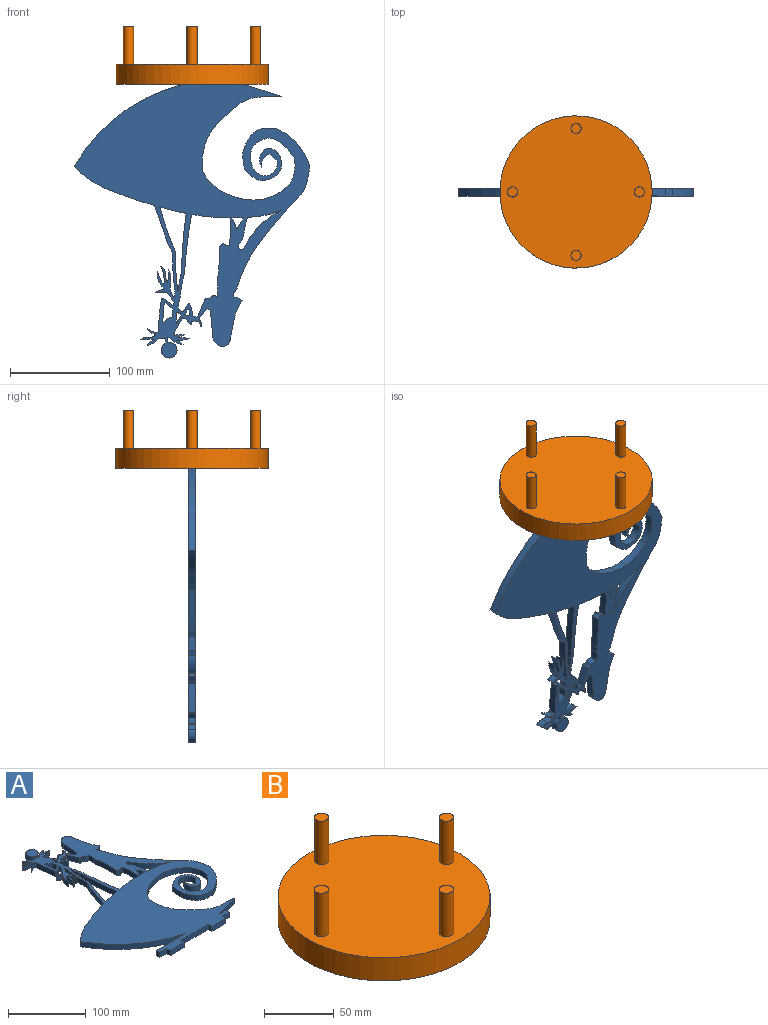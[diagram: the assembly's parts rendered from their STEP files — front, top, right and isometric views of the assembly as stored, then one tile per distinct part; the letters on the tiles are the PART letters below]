
ASSEMBLY  parts=2 mates=1
PART A: 176 faces, bbox 235.7x286.5x7.9 mm
  f0: plane 20.52x7.94mm, normal (1,0.08,0), area 163.3mm2, adj f1,f173,f174,f175
  f1: cylinder r=36.86mm len=9.55mm, axis (0,0,-1), area 89.6mm2, adj f0,f2,f174,f175
  f2: cylinder r=43.14mm len=7.94mm, axis (0,0,-1), area 60.5mm2, adj f1,f173,f174,f175
  f3: plane 10.27x7.94mm, normal (1,0,0), area 81.5mm2, adj f4,f166,f174,f175
  f4: plane 7.94x7.71mm, normal (-0.85,-0.52,0), area 71.6mm2, adj f3,f166,f174,f175
  f5: cylinder r=227.24mm len=11.79mm, axis (0,0,-1), area 93.6mm2, adj f6,f167,f174,f175
  f6: cylinder r=44.33mm len=12.07mm, axis (0,0,-1), area 103.8mm2, adj f5,f167,f174,f175
  f7: cylinder r=337.12mm len=43.63mm, axis (0,0,-1), area 366.7mm2, adj f8,f168,f174,f175
  f8: cylinder r=9.96mm len=7.94mm, axis (0,0,-1), area 34.1mm2, adj f7,f9,f174,f175
  f9: cylinder r=196.99mm len=36.66mm, axis (0,0,-1), area 292mm2, adj f8,f10,f174,f175
  f10: cylinder r=415.23mm len=16.03mm, axis (0,0,-1), area 129.1mm2, adj f9,f11,f174,f175
  f11: cylinder r=48.21mm len=7.94mm, axis (0,0,-1), area 61.4mm2, adj f10,f12,f174,f175
  f12: cylinder r=479.52mm len=54.44mm, axis (0,0,-1), area 433.9mm2, adj f11,f13,f174,f175
  f13: cylinder r=227.24mm len=7.94mm, axis (0,0,-1), area 19mm2, adj f12,f168,f174,f175
  f14: plane 17.78x7.94mm, normal (-0.92,-0.38,0), area 152.8mm2, adj f15,f169,f174,f175
  f15: cylinder r=1.27mm len=7.94mm, axis (0,0,-1), area 13.1mm2, adj f14,f16,f174,f175
  f16: plane 7.94x3.29mm, normal (0.12,-0.99,0), area 26.3mm2, adj f15,f17,f174,f175
  f17: cylinder r=5.3mm len=7.94mm, axis (0,0,-1), area 69.4mm2, adj f16,f18,f174,f175
  f18: cylinder r=24.79mm len=10.48mm, axis (0,0,-1), area 83.9mm2, adj f17,f19,f174,f175
  f19: cylinder r=16.53mm len=7.94mm, axis (0,0,-1), area 44mm2, adj f18,f20,f174,f175
  f20: cylinder r=158.24mm len=34.32mm, axis (0,0,-1), area 273.3mm2, adj f19,f21,f174,f175
  f21: cylinder r=9.12mm len=7.94mm, axis (0,0,-1), area 41.4mm2, adj f20,f22,f174,f175
  f22: cylinder r=7mm len=7.94mm, axis (0,0,-1), area 52.5mm2, adj f21,f23,f174,f175
  f23: cylinder r=99.7mm len=27.95mm, axis (0,0,-1), area 222.8mm2, adj f22,f24,f174,f175
  f24: cylinder r=227.24mm len=38.58mm, axis (0,0,-1), area 307.8mm2, adj f23,f25,f174,f175
  f25: cylinder r=488.64mm len=56.23mm, axis (0,0,-1), area 450mm2, adj f24,f26,f174,f175
  f26: cylinder r=37.95mm len=7.94mm, axis (0,0,-1), area 50mm2, adj f25,f27,f174,f175
  f27: cylinder r=89.95mm len=19.2mm, axis (0,0,-1), area 155mm2, adj f26,f28,f174,f175
  f28: cylinder r=46.77mm len=13.1mm, axis (0,0,-1), area 105.7mm2, adj f27,f29,f174,f175
  f29: plane 7.94x3.21mm, normal (0.58,-0.81,0), area 31.3mm2, adj f28,f30,f174,f175
  f30: cylinder r=1.57mm len=7.94mm, axis (0,0,-1), area 20.4mm2, adj f29,f31,f174,f175
  f31: plane 7.94x7.65mm, normal (-0.85,-0.52,0), area 71.1mm2, adj f30,f32,f174,f175
  f32: cylinder r=0.51mm len=7.94mm, axis (0,0,-1), area 8.2mm2, adj f31,f33,f174,f175
  f33: cylinder r=19.29mm len=12.67mm, axis (0,0,-1), area 105mm2, adj f32,f169,f174,f175
  f34: cylinder r=352.42mm len=52.1mm, axis (0,0,-1), area 538.1mm2, adj f35,f170,f174,f175
  f35: cylinder r=120.39mm len=36.06mm, axis (0,0,-1), area 316.5mm2, adj f34,f36,f174,f175
  f36: cylinder r=14.19mm len=7.94mm, axis (0,0,-1), area 44.1mm2, adj f35,f37,f174,f175
  f37: cylinder r=9.85mm len=7.94mm, axis (0,0,-1), area 44.6mm2, adj f36,f38,f174,f175
  f38: cylinder r=14.52mm len=9.3mm, axis (0,0,-1), area 81.1mm2, adj f37,f39,f174,f175
  f39: cylinder r=0.25mm len=7.94mm, axis (0,0,-1), area 3mm2, adj f38,f40,f174,f175
  f40: cylinder r=40.75mm len=17.83mm, axis (0,0,-1), area 157.1mm2, adj f39,f41,f174,f175
  f41: plane 21.3x7.94mm, normal (0.98,0.18,0), area 172.1mm2, adj f40,f42,f174,f175
  f42: cylinder r=7.87mm len=11.54mm, axis (0,0,-1), area 118.1mm2, adj f41,f43,f174,f175
  f43: cylinder r=11.53mm len=9.08mm, axis (0,0,-1), area 89.5mm2, adj f42,f44,f174,f175
  f44: plane 26.31x7.94mm, normal (-1,0.09,0), area 209.7mm2, adj f43,f45,f174,f175
  f45: cylinder r=6.34mm len=7.94mm, axis (0,0,-1), area 30.2mm2, adj f44,f46,f174,f175
  f46: plane 9.22x7.94mm, normal (0.79,0.62,0), area 93.1mm2, adj f45,f47,f174,f175
  f47: cylinder r=2.32mm len=7.94mm, axis (0,0,-1), area 26.8mm2, adj f46,f48,f174,f175
  f48: cylinder r=5.13mm len=7.94mm, axis (0,0,-1), area 48.7mm2, adj f47,f49,f174,f175
  f49: cylinder r=0.25mm len=7.94mm, axis (0,0,-1), area 5.2mm2, adj f48,f50,f174,f175
  f50: cylinder r=8.39mm len=7.94mm, axis (0,0,-1), area 39.4mm2, adj f49,f51,f174,f175
  f51: cylinder r=2.08mm len=7.94mm, axis (0,0,-1), area 8mm2, adj f50,f52,f174,f175
  f52: cylinder r=8.25mm len=7.94mm, axis (0,0,-1), area 44.8mm2, adj f51,f53,f174,f175
  f53: cylinder r=1.21mm len=7.94mm, axis (0,0,-1), area 13.3mm2, adj f52,f54,f174,f175
  f54: cylinder r=4.68mm len=7.94mm, axis (0,0,-1), area 12.8mm2, adj f53,f55,f174,f175
  f55: cylinder r=0.25mm len=7.94mm, axis (0,0,-1), area 5mm2, adj f54,f56,f174,f175
  f56: cylinder r=7.88mm len=7.94mm, axis (0,0,-1), area 43.2mm2, adj f55,f57,f174,f175
  f57: cylinder r=6.68mm len=7.94mm, axis (0,0,-1), area 47.5mm2, adj f56,f58,f174,f175
  f58: plane 14.05x8.18mm, normal (0.86,0.5,0), area 129mm2, adj f57,f59,f174,f175
  f59: cylinder r=4.51mm len=7.94mm, axis (0,0,-1), area 31.1mm2, adj f58,f60,f174,f175
  f60: cylinder r=20.93mm len=9.94mm, axis (0,0,-1), area 80.1mm2, adj f59,f61,f174,f175
  f61: cylinder r=25.41mm len=7.94mm, axis (0,0,-1), area 56.6mm2, adj f60,f62,f174,f175
  f62: cylinder r=36.23mm len=11.63mm, axis (0,0,-1), area 92.8mm2, adj f61,f63,f174,f175
  f63: cylinder r=28.67mm len=13.4mm, axis (0,0,-1), area 108.3mm2, adj f62,f64,f174,f175
  f64: cylinder r=20.22mm len=7.94mm, axis (0,0,-1), area 66.6mm2, adj f63,f65,f174,f175
  f65: cylinder r=12.82mm len=9.56mm, axis (0,0,-1), area 82.4mm2, adj f64,f66,f174,f175
  f66: cylinder r=11.48mm len=7.94mm, axis (0,0,-1), area 55.9mm2, adj f65,f67,f174,f175
  f67: cylinder r=12.66mm len=7.94mm, axis (0,0,-1), area 38.3mm2, adj f66,f68,f174,f175
  f68: cylinder r=7.89mm len=15.77mm, axis (0,0,-1), area 375.3mm2, adj f67,f69,f174,f175
  f69: cylinder r=14.9mm len=7.94mm, axis (0,0,-1), area 33.3mm2, adj f68,f70,f174,f175
  f70: plane 7.94x7.28mm, normal (0.02,1,0), area 57.8mm2, adj f69,f71,f174,f175
  f71: cylinder r=20.94mm len=10.93mm, axis (0,0,-1), area 102.6mm2, adj f70,f72,f174,f175
  f72: cylinder r=11.14mm len=7.94mm, axis (0,0,-1), area 60.5mm2, adj f71,f73,f174,f175
  f73: cylinder r=0.83mm len=7.94mm, axis (0,0,-1), area 19.2mm2, adj f72,f74,f174,f175
  f74: cylinder r=57.07mm len=11.86mm, axis (0,0,-1), area 94.5mm2, adj f73,f75,f174,f175
  f75: cylinder r=8.74mm len=7.94mm, axis (0,0,-1), area 66.6mm2, adj f74,f76,f174,f175
  f76: cylinder r=10.18mm len=7.94mm, axis (0,0,-1), area 51.8mm2, adj f75,f77,f174,f175
  f77: cylinder r=1.22mm len=7.94mm, axis (0,0,-1), area 23.7mm2, adj f76,f78,f174,f175
  f78: cylinder r=10.13mm len=7.94mm, axis (0,0,-1), area 72.3mm2, adj f77,f79,f174,f175
  f79: cylinder r=23.9mm len=9.43mm, axis (0,0,-1), area 82mm2, adj f78,f80,f174,f175
  f80: cylinder r=1.6mm len=7.94mm, axis (0,0,-1), area 21.9mm2, adj f79,f81,f174,f175
  f81: cylinder r=285.45mm len=31.77mm, axis (0,0,-1), area 253.3mm2, adj f80,f82,f174,f175
  f82: cylinder r=1.27mm len=7.94mm, axis (0,0,-1), area 20.6mm2, adj f81,f83,f174,f175
  f83: plane 10.37x7.94mm, normal (0.58,-0.81,0), area 101.1mm2, adj f82,f84,f174,f175
  f84: cylinder r=70.21mm len=7.94mm, axis (0,0,-1), area 24.5mm2, adj f83,f85,f174,f175
  f85: cylinder r=50.8mm len=10.09mm, axis (0,0,-1), area 99.4mm2, adj f84,f86,f174,f175
  f86: plane 10.81x7.94mm, normal (0,1,0), area 85.8mm2, adj f85,f87,f174,f175
  f87: cylinder r=8.25mm len=7.94mm, axis (0,0,-1), area 56.7mm2, adj f86,f88,f174,f175
  f88: cylinder r=1.04mm len=7.94mm, axis (0,0,-1), area 19.5mm2, adj f87,f89,f174,f175
  f89: cylinder r=20mm len=16.63mm, axis (0,0,-1), area 144mm2, adj f88,f90,f174,f175
  f90: cylinder r=75.46mm len=11.84mm, axis (0,0,-1), area 102mm2, adj f89,f91,f174,f175
  f91: cylinder r=0.82mm len=7.94mm, axis (0,0,-1), area 16.9mm2, adj f90,f92,f174,f175
  f92: cylinder r=35.56mm len=16.89mm, axis (0,0,-1), area 137.6mm2, adj f91,f93,f174,f175
  f93: cylinder r=9.62mm len=7.94mm, axis (0,0,-1), area 59.7mm2, adj f92,f94,f174,f175
  f94: cylinder r=29.77mm len=7.94mm, axis (0,0,-1), area 52.9mm2, adj f93,f95,f174,f175
  f95: cylinder r=10.97mm len=7.94mm, axis (0,0,-1), area 32.8mm2, adj f94,f96,f174,f175
  f96: cylinder r=43.01mm len=12.61mm, axis (0,0,-1), area 101.1mm2, adj f95,f97,f174,f175
  f97: cylinder r=12.3mm len=7.94mm, axis (0,0,-1), area 51.1mm2, adj f96,f98,f174,f175
  f98: cylinder r=141.13mm len=14.24mm, axis (0,0,-1), area 113.2mm2, adj f97,f99,f174,f175
  f99: cylinder r=36.5mm len=7.94mm, axis (0,0,-1), area 63.6mm2, adj f98,f100,f174,f175
  f100: cylinder r=3.1mm len=7.94mm, axis (0,0,-1), area 20.6mm2, adj f99,f101,f174,f175
  f101: cylinder r=70.21mm len=7.94mm, axis (0,0,-1), area 43.9mm2, adj f100,f102,f174,f175
  f102: cylinder r=261.17mm len=37.18mm, axis (0,0,-1), area 295.8mm2, adj f101,f103,f174,f175
  f103: cylinder r=55.57mm len=11.58mm, axis (0,0,-1), area 102.5mm2, adj f102,f104,f174,f175
  f104: plane 35.51x12.47mm, normal (-0.94,0.33,0), area 298.7mm2, adj f103,f105,f174,f175
  f105: cylinder r=445.39mm len=49.93mm, axis (0,0,-1), area 420.4mm2, adj f104,f106,f174,f175
  f106: cylinder r=85.22mm len=30.36mm, axis (0,0,-1), area 298.1mm2, adj f105,f107,f174,f175
  f107: cylinder r=172.99mm len=108.34mm, axis (0,0,-1), area 1109.1mm2, adj f106,f108,f174,f175
  f108: plane 54x7.94mm, normal (0,1,0), area 428.6mm2, adj f107,f109,f174,f175
  f109: plane 7.94x6.35mm, normal (-1,0,0), area 50.4mm2, adj f108,f110,f174,f175
  f110: plane 12.7x7.94mm, normal (0,-1,0), area 100.8mm2, adj f109,f111,f174,f175
  f111: plane 7.94x6.35mm, normal (-1,0,0), area 50.4mm2, adj f110,f112,f174,f175
  f112: plane 25.4x7.94mm, normal (0,-1,0), area 201.6mm2, adj f111,f113,f174,f175
  f113: plane 7.94x6.35mm, normal (1,0,0), area 50.4mm2, adj f112,f114,f174,f175
  f114: plane 50.8x7.94mm, normal (0,-1,0), area 403.2mm2, adj f113,f115,f174,f175
  f115: plane 7.94x6.35mm, normal (-1,0,0), area 50.4mm2, adj f114,f116,f174,f175
  f116: plane 25.4x7.94mm, normal (0,-1,0), area 201.6mm2, adj f115,f117,f174,f175
  f117: plane 7.94x6.35mm, normal (1,0,0), area 50.4mm2, adj f116,f118,f174,f175
  f118: plane 12.7x7.94mm, normal (0,-1,0), area 100.8mm2, adj f117,f119,f174,f175
  f119: plane 7.94x6.35mm, normal (1,0,0), area 50.4mm2, adj f118,f120,f174,f175
  f120: plane 11.56x7.94mm, normal (0,1,0), area 91.8mm2, adj f119,f121,f174,f175
  f121: plane 38.12x11.95mm, normal (0.3,-0.95,0), area 317.1mm2, adj f120,f122,f174,f175
  f122: plane 21.78x7.94mm, normal (0.03,1,0), area 173mm2, adj f121,f123,f174,f175
  f123: cylinder r=37.94mm len=21.74mm, axis (0,0,-1), area 186.1mm2, adj f122,f124,f174,f175
  f124: cylinder r=179.29mm len=19.92mm, axis (0,0,-1), area 211.2mm2, adj f123,f125,f174,f175
  f125: cylinder r=57.58mm len=49.12mm, axis (0,0,-1), area 424.3mm2, adj f124,f126,f174,f175
  f126: cylinder r=42.38mm len=19.79mm, axis (0,0,-1), area 219.2mm2, adj f125,f127,f174,f175
  f127: cylinder r=79.8mm len=22.23mm, axis (0,0,-1), area 188.1mm2, adj f126,f128,f174,f175
  f128: cylinder r=50.17mm len=15.51mm, axis (0,0,-1), area 123.7mm2, adj f127,f129,f174,f175
  f129: cylinder r=47.79mm len=27.94mm, axis (0,0,-1), area 250.3mm2, adj f128,f130,f174,f175
  f130: cylinder r=25.95mm len=13.94mm, axis (0,0,-1), area 127.2mm2, adj f129,f131,f174,f175
  f131: cylinder r=36.6mm len=14.64mm, axis (0,0,-1), area 117mm2, adj f130,f132,f174,f175
  f132: cylinder r=56.33mm len=16.26mm, axis (0,0,-1), area 177.7mm2, adj f131,f133,f174,f175
  f133: cylinder r=19.27mm len=13.59mm, axis (0,0,-1), area 114mm2, adj f132,f134,f174,f175
  f134: cylinder r=28.7mm len=8.69mm, axis (0,0,-1), area 78.2mm2, adj f133,f135,f174,f175
  f135: cylinder r=16.62mm len=10.59mm, axis (0,0,-1), area 98.7mm2, adj f134,f136,f174,f175
  f136: cylinder r=25.93mm len=10.49mm, axis (0,0,-1), area 84mm2, adj f135,f137,f174,f175
  f137: cylinder r=20.22mm len=7.94mm, axis (0,0,-1), area 66.2mm2, adj f136,f138,f174,f175
  f138: cylinder r=12.6mm len=16.26mm, axis (0,0,-1), area 142.9mm2, adj f137,f139,f174,f175
  f139: cylinder r=12.31mm len=12.9mm, axis (0,0,-1), area 119.4mm2, adj f138,f140,f174,f175
  f140: cylinder r=38.53mm len=7.94mm, axis (0,0,-1), area 78.2mm2, adj f139,f141,f174,f175
  f141: cylinder r=10.76mm len=12.96mm, axis (0,0,-1), area 136.7mm2, adj f140,f142,f174,f175
  f142: cylinder r=12.51mm len=16.18mm, axis (0,0,-1), area 140.2mm2, adj f141,f143,f174,f175
  f143: cylinder r=8.34mm len=8.05mm, axis (0,0,-1), area 69.3mm2, adj f142,f144,f174,f175
  f144: cylinder r=13.73mm len=9.03mm, axis (0,0,-1), area 97.6mm2, adj f143,f145,f174,f175
  f145: cylinder r=17.66mm len=11.91mm, axis (0,0,-1), area 96.7mm2, adj f144,f146,f174,f175
  f146: cylinder r=15.3mm len=10.2mm, axis (0,0,-1), area 114.6mm2, adj f145,f147,f174,f175
  f147: cylinder r=26.76mm len=12.66mm, axis (0,0,-1), area 102.1mm2, adj f146,f148,f174,f175
  f148: cylinder r=32.43mm len=13.82mm, axis (0,0,-1), area 135.4mm2, adj f147,f149,f174,f175
  f149: cylinder r=52.04mm len=17.76mm, axis (0,0,-1), area 142.9mm2, adj f148,f150,f174,f175
  f150: cylinder r=51.61mm len=14.68mm, axis (0,0,-1), area 127.1mm2, adj f149,f151,f174,f175
  f151: cylinder r=20.92mm len=11.08mm, axis (0,0,-1), area 114.4mm2, adj f150,f152,f174,f175
  f152: cylinder r=45.16mm len=14.96mm, axis (0,0,-1), area 119.5mm2, adj f151,f153,f174,f175
  f153: cylinder r=50.49mm len=13.17mm, axis (0,0,-1), area 118.6mm2, adj f152,f154,f174,f175
  f154: cylinder r=57.88mm len=31.34mm, axis (0,0,-1), area 307.7mm2, adj f153,f155,f174,f175
  f155: cylinder r=105.54mm len=23.2mm, axis (0,0,-1), area 189mm2, adj f154,f170,f174,f175
  f156: cylinder r=9.54mm len=7.94mm, axis (0,0,-1), area 55.6mm2, adj f157,f171,f174,f175
  f157: plane 7.94x5.45mm, normal (0.86,0.5,0), area 50.1mm2, adj f156,f171,f174,f175
  f158: cylinder r=80.87mm len=35.9mm, axis (0,0,-1), area 405.8mm2, adj f159,f172,f174,f175
  f159: cylinder r=60.69mm len=18.48mm, axis (0,0,-1), area 154.2mm2, adj f158,f160,f174,f175
  f160: cylinder r=227.24mm len=15.36mm, axis (0,0,-1), area 122.6mm2, adj f159,f161,f174,f175
  f161: cylinder r=109.18mm len=17.03mm, axis (0,0,-1), area 138.9mm2, adj f160,f162,f174,f175
  f162: cylinder r=28.03mm len=7.94mm, axis (0,0,-1), area 53.5mm2, adj f161,f163,f174,f175
  f163: cylinder r=21.61mm len=7.94mm, axis (0,0,-1), area 44.5mm2, adj f162,f164,f174,f175
  f164: cylinder r=2.54mm len=7.94mm, axis (0,0,-1), area 15mm2, adj f163,f165,f174,f175
  f165: cylinder r=7.26mm len=7.94mm, axis (0,0,-1), area 34.9mm2, adj f164,f172,f174,f175
  f166: cylinder r=4.71mm len=7.94mm, axis (0,0,-1), area 45.2mm2, adj f3,f4,f174,f175
  f167: cylinder r=82.29mm len=12.41mm, axis (0,0,-1), area 112.8mm2, adj f5,f6,f174,f175
  f168: cylinder r=445.39mm len=24.08mm, axis (0,0,-1), area 196.7mm2, adj f7,f13,f174,f175
  f169: cylinder r=21.13mm len=7.94mm, axis (0,0,-1), area 44.3mm2, adj f14,f33,f174,f175
  f170: cylinder r=60.69mm len=8.89mm, axis (0,0,-1), area 91.9mm2, adj f34,f155,f174,f175
  f171: cylinder r=8.45mm len=7.94mm, axis (0,0,-1), area 37.5mm2, adj f156,f157,f174,f175
  f172: cylinder r=25.34mm len=7.94mm, axis (0,0,-1), area 45.7mm2, adj f158,f165,f174,f175
  f173: plane 8.95x7.94mm, normal (-0.62,0.79,0), area 90.4mm2, adj f0,f2,f174,f175
  f174: plane 286.54x235.68mm, normal (0,0,1), area 23375.6mm2, adj f0,f1,f2,f3,f4,f5,f6,f7
  f175: plane 286.54x235.68mm, normal (0,0,-1), area 23375.6mm2, adj f0,f1,f2,f3,f4,f5,f6,f7
PART B: 24 faces, bbox 152.4x152.4x58.4 mm
  f0: plane 152.4x152.4mm, normal (0,0,-1), area 17172mm2, adj f1,f4,f6,f7,f8
  f1: cylinder r=76.2mm len=152.4mm, axis (0,0,-1), area 9728.8mm2, adj f0,f2
  f2: plane 152.4x152.4mm, normal (0,0,1), area 17917.2mm2, adj f1,f16,f18,f20,f22
  f3: plane 50.04x8.18mm, normal (0,0,-1), area 409.1mm2, adj f6,f7,f10,f14
  f4: plane 8.18x6.54mm, normal (1,0,0), area 53.5mm2, adj f0,f5,f6,f7
  f5: plane 14.22x8.18mm, normal (0,0,-1), area 116.3mm2, adj f4,f6,f7,f13
  f6: plane 130.81x13.08mm, normal (0,1,0), area 1197.8mm2, adj f0,f3,f4,f5,f8,f9,f10,f11
  f7: plane 130.81x13.08mm, normal (0,-1,0), area 1197.8mm2, adj f0,f3,f4,f5,f8,f9,f10,f11
  f8: plane 8.18x6.54mm, normal (-1,0,0), area 53.5mm2, adj f0,f6,f7,f9
  f9: plane 14.22x8.18mm, normal (0,0,-1), area 116.3mm2, adj f6,f7,f8,f11
  f10: plane 8.18x6.54mm, normal (1,0,0), area 53.5mm2, adj f3,f6,f7,f12
  f11: plane 8.18x6.54mm, normal (-1,0,0), area 53.5mm2, adj f6,f7,f9,f12
  f12: plane 26.16x8.18mm, normal (0,0,-1), area 213.9mm2, adj f6,f7,f10,f11
  f13: plane 8.18x6.54mm, normal (1,0,0), area 53.5mm2, adj f5,f6,f7,f15
  f14: plane 8.18x6.54mm, normal (-1,0,0), area 53.5mm2, adj f3,f6,f7,f15
  f15: plane 26.16x8.18mm, normal (0,0,-1), area 213.9mm2, adj f6,f7,f13,f14
  f16: cylinder r=5.08mm len=38.1mm, axis (0,0,-1), area 1216.1mm2, adj f2,f17
  f17: plane 10.16x10.16mm, normal (0,0,1), area 81.1mm2, adj f16
  f18: cylinder r=5.08mm len=38.1mm, axis (0,0,-1), area 1216.1mm2, adj f2,f19
  f19: plane 10.16x10.16mm, normal (0,0,1), area 81.1mm2, adj f18
  f20: cylinder r=5.08mm len=38.1mm, axis (0,0,-1), area 1216.1mm2, adj f2,f21
  f21: plane 10.16x10.16mm, normal (0,0,1), area 81.1mm2, adj f20
  f22: cylinder r=5.08mm len=38.1mm, axis (0,0,-1), area 1216.1mm2, adj f2,f23
  f23: plane 10.16x10.16mm, normal (0,0,1), area 81.1mm2, adj f22
PLACE A rot(axis=(-1,0,0),90deg) t=(9.68,-3.97,-177.91)mm
PLACE B at identity fixed
MATE fastened A.f114 <-> B.f1  axis (0,0,1) through (0,0,6.35)mm
